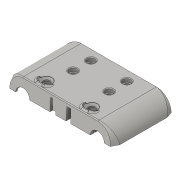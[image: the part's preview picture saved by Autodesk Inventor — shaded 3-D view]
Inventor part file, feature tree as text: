
AUTODESK INVENTOR PART (.ipt)
format: ipt  version: 2016 (Build 200138000, 138)  size: 1,002,496 bytes
history: native  units: in
note: dims shown in document units (in); Inventor stores cm internally (conversion verified against a paired STEP export)
features: extrude x1, sketch x1, imported_body x1
ambient origin geometry x8: Origin, YZ Plane, XZ Plane, XY Plane, X Axis, Y Axis, Z Axis, Center Point
bodies: Solid1 (feature_tree)
feature tree (3):
  extrude  "Extrusion1"  Depth=0.3937in
  sketch  "Sketch1"  dims[d0=0.0098in d1=0.3937in d2=0.0069in]
  imported_body  "Base1"
